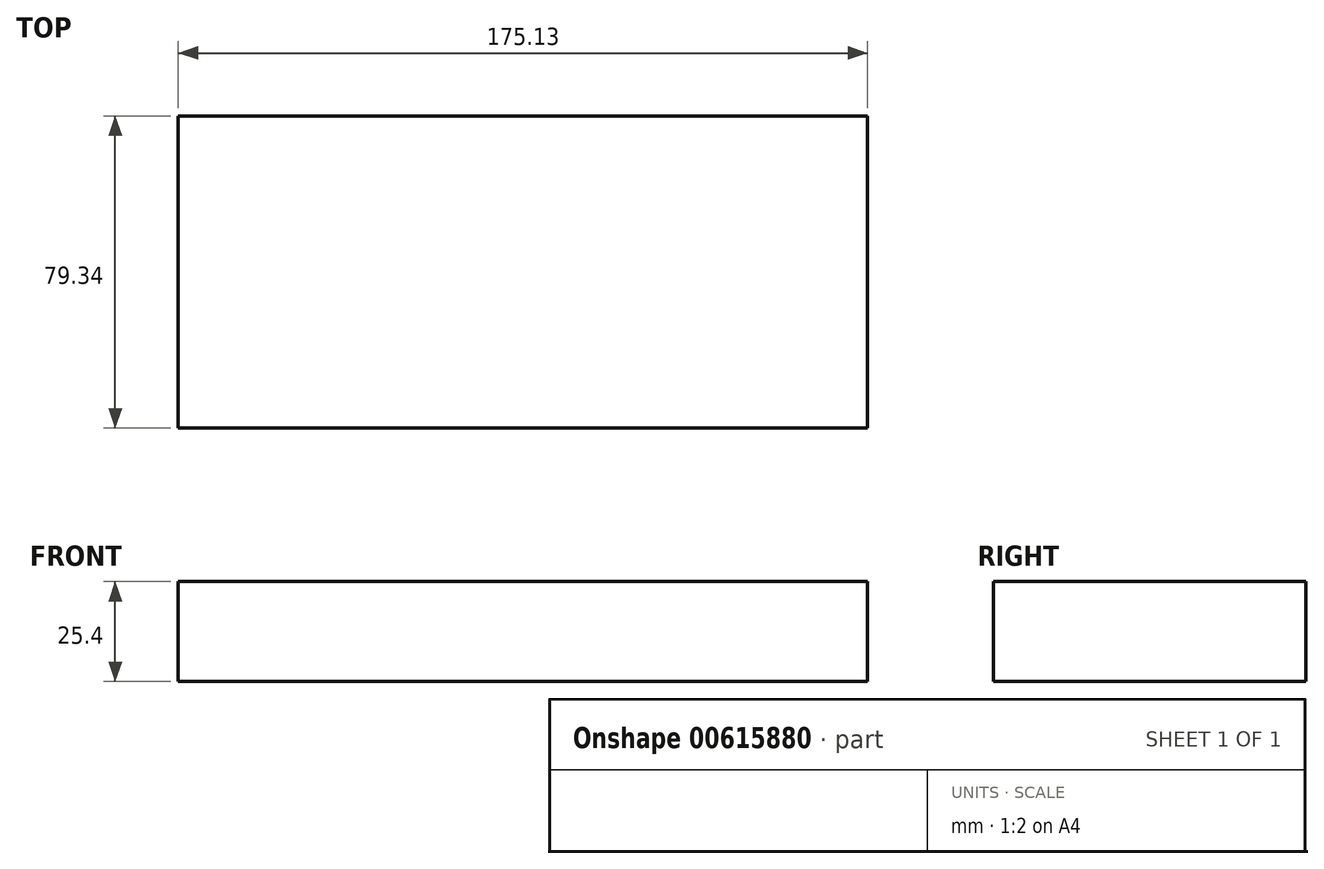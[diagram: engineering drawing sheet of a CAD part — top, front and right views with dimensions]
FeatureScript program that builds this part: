
annotation { "Feature Type Name" : "Feature", "Feature Type Description" : "" }
export const myFeature = defineFeature(function(context is Context, id is Id, definition is map)
    precondition{}
    {
        {
            var Q0;
            Q0=qCreatedBy(makeId("Top.planeOp"),FACE);
            var sketch = newSketch(context, id + "F0", { "sketchPlane" : qUnion([Q0])});
            skLineSegment(sketch, "E0.bottom", {"start": v(-116.57, -53.12) * mm, "end": v(58.56, -53.12) * mm});
            skLineSegment(sketch, "E0.top", {"start": v(-116.57, 26.22) * mm, "end": v(58.56, 26.22) * mm});
            skLineSegment(sketch, "E0.left", {"start": v(-116.57, -53.12) * mm, "end": v(-116.57, 26.22) * mm});
            skLineSegment(sketch, "E0.right", {"start": v(58.56, -53.12) * mm, "end": v(58.56, 26.22) * mm});
            skSolve(sketch);
        }
        {
            var Q0;
            Q0=makeQuery(id+"F0.imprint","IMPRINT",FACE,{"disambiguationData":[TD([[makeQuery(id+"F0.imprint","IMPRINT",EDGE,{"derivedFrom":sQuery(id+"F0.wireOp",EDGE,"E0.bottom")}),1.0]])]});
            extrude(context, id + "F1", {"entities" : qUnion([Q0]), "depth" : 25.4 * mm, "offsetDistance" : 25.4 * mm});
        }
    });
